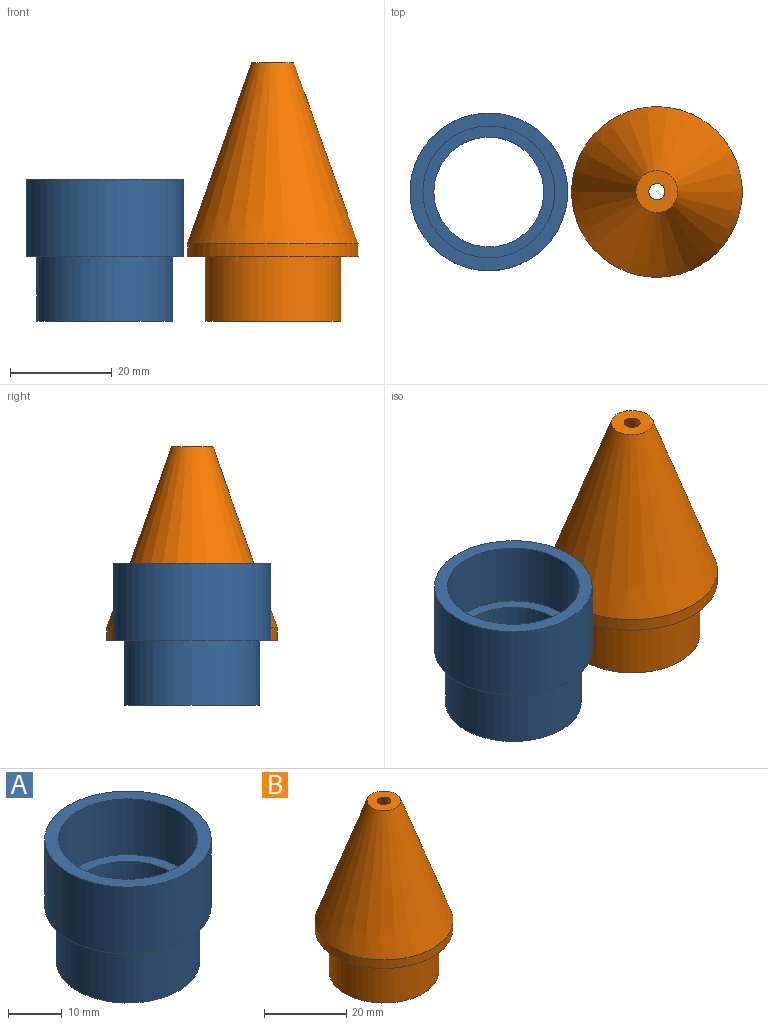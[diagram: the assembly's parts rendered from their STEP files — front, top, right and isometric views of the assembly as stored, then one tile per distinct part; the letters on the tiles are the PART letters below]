
ASSEMBLY  parts=2 mates=1
PART A: 8 faces, bbox 31x31x27.9 mm
  f0: cylinder r=12.95mm len=25.91mm, axis (0,0,-1), area 1033.7mm2, adj f1,f7
  f1: plane 25.91x25.91mm, normal (0,0,1), area 161.1mm2, adj f0,f2
  f2: cylinder r=10.79mm len=21.59mm, axis (0,0,-1), area 1033.7mm2, adj f1,f3
  f3: plane 26.67x26.67mm, normal (0,0,-1), area 192.5mm2, adj f2,f4
  f4: cylinder r=13.33mm len=26.67mm, axis (0,0,-1), area 1064.1mm2, adj f3,f5
  f5: plane 30.99x30.99mm, normal (0,0,-1), area 195.5mm2, adj f4,f6
  f6: cylinder r=15.49mm len=30.99mm, axis (0,0,-1), area 1483.6mm2, adj f5,f7
  f7: plane 30.99x30.99mm, normal (0,0,1), area 227mm2, adj f0,f6
PART B: 9 faces, bbox 33.5x33.5x50.8 mm
  f0: cone r=1.59mm half-angle=19.6deg, axis (0,0,-1), area 1874.6mm2, adj f1,f8
  f1: plane 28.45x28.45mm, normal (0,0,1), area 269.5mm2, adj f0,f2
  f2: cylinder r=10.79mm len=21.59mm, axis (0,0,-1), area 1033.7mm2, adj f1,f3
  f3: plane 26.67x26.67mm, normal (0,0,-1), area 192.5mm2, adj f2,f4
  f4: cylinder r=13.33mm len=26.67mm, axis (0,0,-1), area 1064.1mm2, adj f3,f5
  f5: plane 33.53x33.53mm, normal (0,0,-1), area 324.2mm2, adj f4,f6
  f6: cylinder r=16.76mm len=33.53mm, axis (0,0,-1), area 267.5mm2, adj f5,f7
  f7: cone r=16.76mm half-angle=19.6deg, axis (0,0,-1), area 2476.9mm2, adj f6,f8
  f8: plane 8.26x8.26mm, normal (0,0,1), area 45.6mm2, adj f0,f7
PLACE A t=(8.6,16.05,2.66)mm
PLACE B t=(41.62,16.05,2.66)mm
MATE fastened B.f0 <-> A.f3  axis (0,0,-1) through (41.62,16.05,2.66)mm
